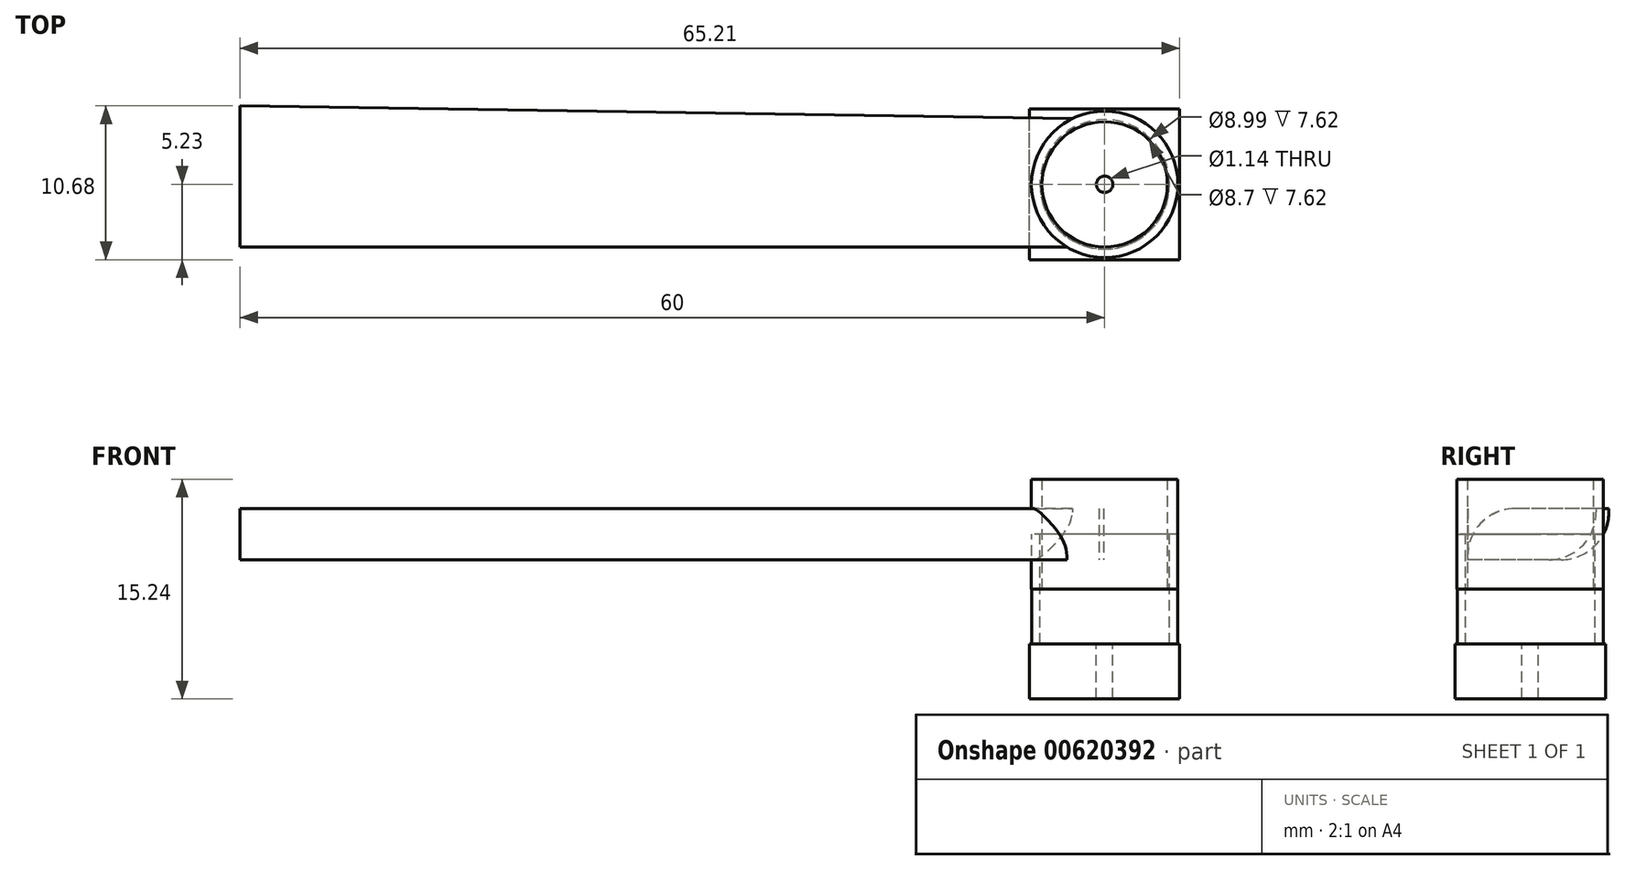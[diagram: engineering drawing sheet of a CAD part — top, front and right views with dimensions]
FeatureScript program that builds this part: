
annotation { "Feature Type Name" : "Feature", "Feature Type Description" : "" }
export const myFeature = defineFeature(function(context is Context, id is Id, definition is map)
    precondition{}
    {
        {
            var Q0;
            Q0=qCreatedBy(makeId("Top.planeOp"),FACE);
            var sketch = newSketch(context, id + "F0", { "sketchPlane" : qUnion([Q0])});
            skCircle(sketch, "E0", {"center": v(0, 0) * mm, "radius": 4.35 * mm});
            skCircle(sketch, "E1", {"center": v(0, 0) * mm, "radius": 5.08 * mm});
            skSolve(sketch);
        }
        {
            var Q0;
            Q0=qSketchRegion(id+"F0",true);
            extrude(context, id + "F1", {"entities" : qUnion([Q0]), "depth" : 3.8 * mm});
        }
        {
            var Q0;
            Q0=qSketchRegion(id+"F0",true);
            var Q1;
            Q1=makeQuery(id+"F1.opExtrude","CAP_FACE",FACE,{"disambiguationData":[OSD([sQuery(id+"F0.wireOp",EDGE,"E0"),sQuery(id+"F0.wireOp",EDGE,"E1")])],"isStart":true});
            extrude(context, id + "F2", {"entities" : qUnion([Q0, Q1]), "operationType" : NewBodyOperationType.ADD, "oppositeDirection" : true, "depth" : 3.8 * mm});
        }
        {
            var Q0;
            Q0=qCreatedBy(makeId("Top.planeOp"),FACE);
            var sketch = newSketch(context, id + "F3", { "sketchPlane" : qUnion([Q0])});
            skLineSegment(sketch, "E2", {"start": v(0, 0) * mm, "end": v(-5.07, 0) * mm});
            skLineSegment(sketch, "E3", {"start": v(0, -4.35) * mm, "end": v(-60, -4.35) * mm});
            skLineSegment(sketch, "E4", {"start": v(-60, -4.35) * mm, "end": v(-55.05, -4.35) * mm});
            skLineSegment(sketch, "E5", {"start": v(-60, 5.45) * mm, "end": v(-60, -4.35) * mm});
            skLineSegment(sketch, "E6", {"start": v(-5.07, 0) * mm, "end": v(-2.72, -4.2) * mm});
            skLineSegment(sketch, "E7", {"start": v(-5.07, 0) * mm, "end": v(-2.52, 4.3) * mm});
            skLineSegment(sketch, "E8", {"start": v(-2.72, -4.2) * mm, "end": v(0, -4.35) * mm});
            skLineSegment(sketch, "E9", {"start": v(-60, 5.45) * mm, "end": v(0, 4.52) * mm});
            skLineSegment(sketch, "E10", {"start": v(-2.52, 4.3) * mm, "end": v(0, 4.52) * mm});
            skLineSegment(sketch, "E11", {"start": v(0, 4.52) * mm, "end": v(0, -4.35) * mm});
            skSolve(sketch);
        }
        {
            var Q0;
            Q0=makeQuery(id+"F3.imprint","IMPRINT",FACE,{"disambiguationData":[TD([[makeQuery(id+"F3.imprint","IMPRINT",EDGE,{"derivedFrom":sQuery(id+"F3.wireOp",EDGE,"E3")}),-1.0]])]});
            extrude(context, id + "F4", {"entities" : qUnion([Q0]), "operationType" : NewBodyOperationType.ADD, "depth" : 1.78 * mm});
        }
        {
            var Q0;
            Q0=makeQuery(id+"F3.imprint","IMPRINT",FACE,{"disambiguationData":[TD([[makeQuery(id+"F3.imprint","IMPRINT",EDGE,{"derivedFrom":sQuery(id+"F3.wireOp",EDGE,"E3")}),-1.0]])]});
            extrude(context, id + "F5", {"entities" : qUnion([Q0]), "operationType" : NewBodyOperationType.ADD, "oppositeDirection" : true, "depth" : 1.78 * mm, "offsetDistance" : 25.4 * mm});
        }
        {
            var Q0;
            Q0=qCreatedBy(makeId("Top.planeOp"),FACE);
            var sketch = newSketch(context, id + "F6", { "sketchPlane" : qUnion([Q0])});
            skLineSegment(sketch, "E12", {"start": v(0, 0) * mm, "end": v(-71.02, 0) * mm});
            skLineSegment(sketch, "E13", {"start": v(-50.9, 0) * mm, "end": v(-50.9, -5) * mm});
            skLineSegment(sketch, "E14", {"start": v(-50.9, -5) * mm, "end": v(-50.9, 5.15) * mm});
            skLineSegment(sketch, "E15.bottom", {"start": v(-50.9, 0) * mm, "end": v(0, 0) * mm});
            skLineSegment(sketch, "E15.left", {"start": v(-50.9, 0) * mm, "end": v(-50.9, -1.39) * mm});
            skLineSegment(sketch, "E15.right", {"start": v(0, 0) * mm, "end": v(0, -1.39) * mm});
            skLineSegment(sketch, "E16.MirrorCS", {"start": v(0, 0) * mm, "end": v(0, 1.39) * mm});
            skPoint(sketch, "E17", {"position": v(-58.4, -4.06) * mm});
            skSolve(sketch);
        }
        {
            var Q0;
            Q0=qCreatedBy(makeId("Right.planeOp"),FACE);
            var sketch = newSketch(context, id + "F7", { "sketchPlane" : qUnion([Q0])});
            skCircle(sketch, "E18", {"center": v(0, 0) * mm, "radius": 1.4 * mm});
            skSolve(sketch);
        }
        {
            var Q0;
            Q0=qCreatedBy(makeId("Top.planeOp"),FACE);
            var sketch = newSketch(context, id + "F8", { "sketchPlane" : qUnion([Q0])});
            skCircle(sketch, "E19", {"center": v(0, 0) * mm, "radius": 5.07 * mm});
            skCircle(sketch, "E20", {"center": v(0, 0) * mm, "radius": 4.5 * mm});
            skSolve(sketch);
        }
        {
            var Q0;
            Q0=qSketchRegion(id+"F8",true);
            extrude(context, id + "F9", {"entities" : qUnion([Q0]), "oppositeDirection" : true, "depth" : 11.43 * mm, "offsetDistance" : 25.4 * mm});
        }
        {
            var Q0;
            Q0=makeQuery(id+"F9.opExtrude","CAP_FACE",FACE,{"disambiguationData":[OSD([sQuery(id+"F8.wireOp",EDGE,"E19"),sQuery(id+"F8.wireOp",EDGE,"E20")])],"isStart":false});
            var sketch = newSketch(context, id + "F10", { "sketchPlane" : qUnion([Q0])});
            skLineSegment(sketch, "E21.bottom", {"start": v(-5.2, 5.23) * mm, "end": v(5.2, 5.23) * mm});
            skLineSegment(sketch, "E21.top", {"start": v(-5.2, -5.23) * mm, "end": v(5.2, -5.23) * mm});
            skLineSegment(sketch, "E21.left", {"start": v(-5.2, 5.23) * mm, "end": v(-5.2, -5.23) * mm});
            skLineSegment(sketch, "E21.right", {"start": v(5.2, 5.23) * mm, "end": v(5.2, -5.23) * mm});
            skPoint(sketch, "E21.middle", {"position": v(0, 0) * mm});
            skSolve(sketch);
        }
        {
            var Q0;
            Q0=qSketchRegion(id+"F10",true);
            extrude(context, id + "F11", {"entities" : qUnion([Q0]), "operationType" : NewBodyOperationType.ADD, "oppositeDirection" : true, "depth" : 3.8 * mm});
        }
        {
            var Q0;
            Q0=sQuery(id+"F6.wireOp",VERTEX,"E15.right.start");
            var Q1;
            Q1=makeQuery(id+"F9.opExtrude","SWEPT_BODY",BODY,{"disambiguationData":[OSD([sQuery(id+"F8.wireOp",EDGE,"E19"),sQuery(id+"F8.wireOp",EDGE,"E20")])]});
            hole(context, id + "F12", {"style" : HoleStyle.SIMPLE, "endStyle" : HoleEndStyle.THROUGH, "holeDiameter" : 1.14 * mm, "isTappedThrough" : true, "tappedDepth" : 12.7 * mm, "tapClearance" : 3, "startFromSketch" : true, "locations" : qUnion([Q0]), "scope" : qUnion([Q1]), "majorDiameter" : 6.35 * mm});
        }
        {
            var Q0;
            Q0=makeQuery(id+"Fv6bU5iqls4cmOd_5.opExtrude","CAP_EDGE",EDGE,{"disambiguationData":[OSD([sQuery(id+"F3.wireOp",EDGE,"E4")])],"isStart":false});
            var Q1;
            Q1=makeQuery(id+"F4.opExtrude","CAP_EDGE",EDGE,{"disambiguationData":[OSD([sQuery(id+"F3.wireOp",EDGE,"E3")])],"isStart":false});
            var Q2;
            Q2=makeQuery(id+"F5.opExtrude","CAP_EDGE",EDGE,{"disambiguationData":[OSD([sQuery(id+"F3.wireOp",EDGE,"5d1I3ajL-ww2i-JY2E-9Tbv-LJCMbZyRcHCw")])],"isStart":false});
            var Q3;
            Q3=makeQuery(id+"FenjTYufOAOmaFw_6.opExtrude","CAP_EDGE",EDGE,{"disambiguationData":[OSD([sQuery(id+"F3.wireOp",EDGE,"E5")])],"isStart":false});
            var Q4;
            Q4=makeQuery(id+"F5.opExtrude","CAP_EDGE",EDGE,{"disambiguationData":[OSD([sQuery(id+"F3.wireOp",EDGE,"E9")])],"isStart":false});
            fillet(context, id + "F13", {"entities" : qUnion([Q0, Q1, Q2, Q3, Q4]), "radius" : 3.3 * mm, "tangentPropagation" : true, "allowEdgeOverflow" : false});
        }
    });
